# Revit family: FU_Stool_Sandler_Timber 3-4
name_source: partatom
category: Furniture
units: mm (PartAtom-declared; Revit-internal decimal feet)

## family parameters
Always vertical = Yes
Cut with Voids When Loaded = No
OmniClass Number = 23.40.20.00
OmniClass Title = General Furniture and Specialties
Room Calculation Point = No
Shared = No
Work Plane-Based = No

## types (1)
- Timber 3.4
    Default Elevation = 0 mm  [stored 0 ft]
    Depth = 520 mm  [stored 1.70604 ft]
    Description = Barstool with an upholstered seat and upholstered back panel attached to a wooden back on a solid beech frame fitted with a stainless steel kick-plate on the front footrest.
    Height = 1020 mm  [stored 3.34646 ft]
    Manufacturer = Sandler
    Model = Timber 3.4
    URL = https://www.sandlerseating.com
    Width = 450 mm  [stored 1.47638 ft]

note: [stored X ft] marks values corroborated as IEEE doubles in the binary element streams (Revit-internal decimal feet)

## geometry (parser evidence)
native form markers: Sweep x9
no freeform markers — native parametric forms only
